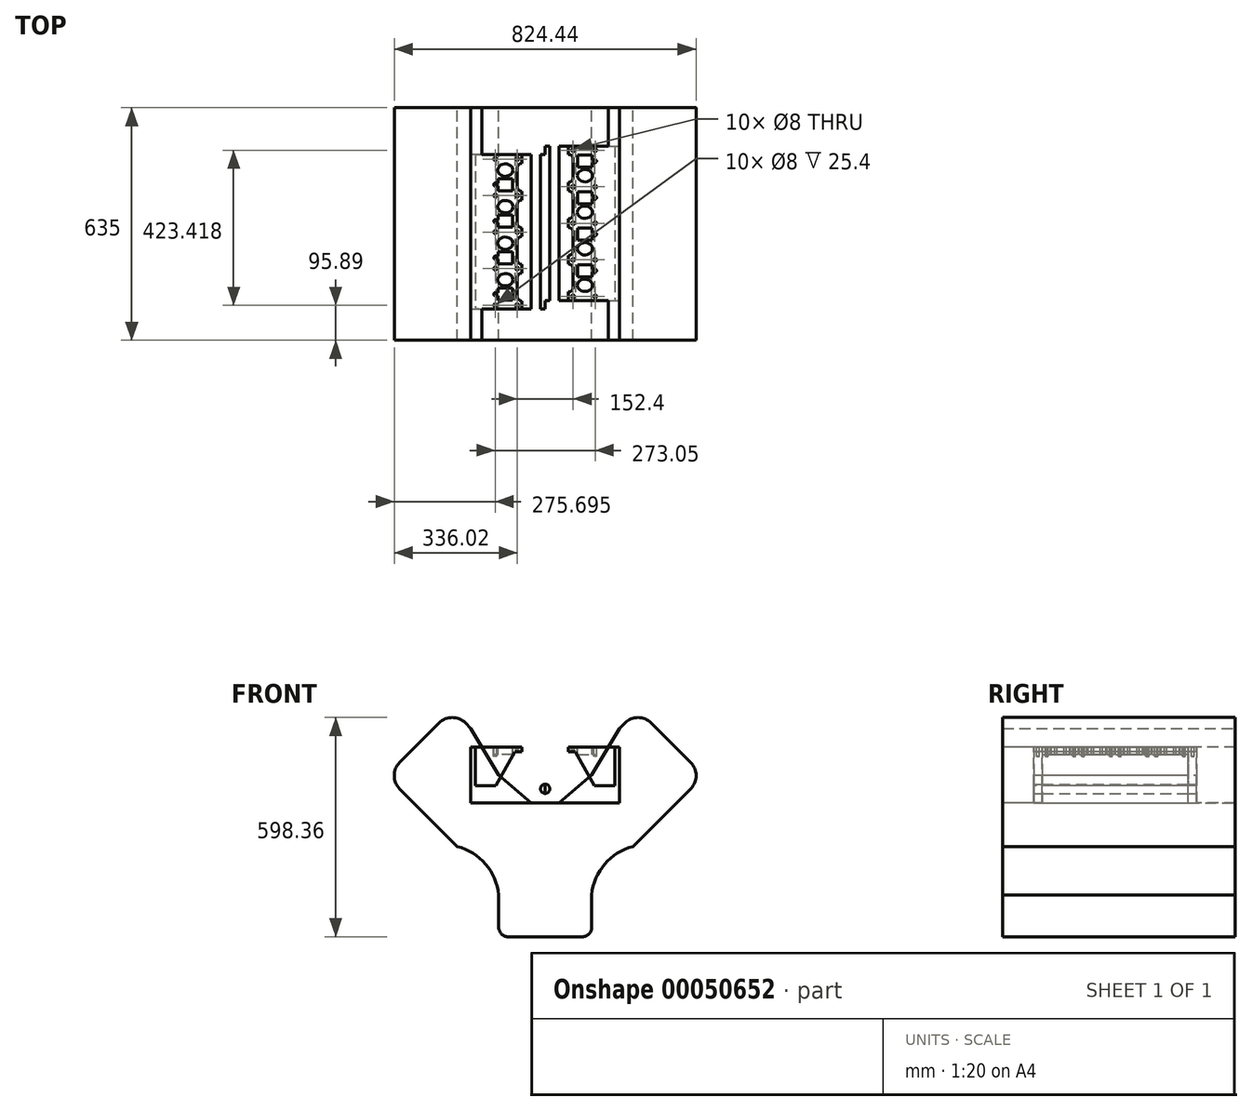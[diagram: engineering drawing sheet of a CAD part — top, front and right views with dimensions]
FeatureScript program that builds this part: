
annotation { "Feature Type Name" : "Feature", "Feature Type Description" : "" }
export const myFeature = defineFeature(function(context is Context, id is Id, definition is map)
    precondition{}
    {
        {
            var Q0;
            Q0=qCreatedBy(makeId("Front.planeOp"),FACE);
            var sketch = newSketch(context, id + "F0", { "sketchPlane" : qUnion([Q0])});
            skLineSegment(sketch, "E0", {"start": v(0, 0) * mm, "end": v(-323.29, 323.29) * mm, "construction": true});
            skLineSegment(sketch, "E1", {"start": v(0, 0) * mm, "end": v(465.39, 465.39) * mm, "construction": true});
            skLineSegment(sketch, "E2", {"start": v(-127, 0) * mm, "end": v(-127, -76.2) * mm});
            skLineSegment(sketch, "E3", {"start": v(-127, -76.2) * mm, "end": v(0, -76.2) * mm, "construction": true});
            skLineSegment(sketch, "E4", {"start": v(-377.17, 269.4) * mm, "end": v(-239.8, 132.03) * mm});
            skLineSegment(sketch, "E5", {"start": v(-203.2, 454.65) * mm, "end": v(-127, 327.65) * mm});
            skLineSegment(sketch, "E6", {"start": v(-127, 327.65) * mm, "end": v(-38.1, 251.45) * mm});
            skLineSegment(sketch, "E7", {"start": v(-38.1, 251.45) * mm, "end": v(0, 251.45) * mm});
            skLineSegment(sketch, "E8", {"start": v(-377.17, 269.4) * mm, "end": v(-397.34, 289.57) * mm});
            skLineSegment(sketch, "E9", {"start": v(-397.34, 361.42) * mm, "end": v(-289.57, 469.18) * mm});
            skLineSegment(sketch, "E10", {"start": v(-203.2, 454.65) * mm, "end": v(-217.73, 469.18) * mm});
            skPoint(sketch, "E11", {"position": v(-323.29, 323.29) * mm});
            skArc(sketch, "E12", {"start": v(-127, 0) * mm, "mid": v(-162.67, 83.72) * mm, "end": v(-239.8, 132.03) * mm});
            skPoint(sketch, "E13.visualSharp", {"position": v(-253.65, 505.1) * mm});
            skArc(sketch, "E13.filletArc", {"start": v(-217.73, 469.18) * mm, "mid": v(-253.65, 484.06) * mm, "end": v(-289.57, 469.18) * mm});
            skPoint(sketch, "E14.visualSharp", {"position": v(-433.26, 325.5) * mm});
            skArc(sketch, "E14.filletArc", {"start": v(-397.34, 361.42) * mm, "mid": v(-412.22, 325.5) * mm, "end": v(-397.34, 289.57) * mm});
            skLineSegment(sketch, "E15.MirrorCS", {"start": v(377.17, 269.4) * mm, "end": v(397.34, 289.57) * mm});
            skLineSegment(sketch, "E16.MirrorCS", {"start": v(203.2, 454.65) * mm, "end": v(217.73, 469.18) * mm});
            skLineSegment(sketch, "E17.MirrorCS", {"start": v(38.1, 251.45) * mm, "end": v(0, 251.45) * mm});
            skArc(sketch, "E18.MirrorCS", {"start": v(217.73, 469.18) * mm, "mid": v(253.65, 484.06) * mm, "end": v(289.57, 469.18) * mm});
            skArc(sketch, "E19.MirrorCS", {"start": v(397.34, 361.42) * mm, "mid": v(412.22, 325.5) * mm, "end": v(397.34, 289.57) * mm});
            skLineSegment(sketch, "E20.MirrorCS", {"start": v(0, 0) * mm, "end": v(323.29, 323.29) * mm, "construction": true});
            skLineSegment(sketch, "E21.MirrorCS", {"start": v(377.17, 269.4) * mm, "end": v(203.2, 454.65) * mm, "construction": true});
            skLineSegment(sketch, "E22.MirrorCS", {"start": v(127, 327.65) * mm, "end": v(38.1, 251.45) * mm});
            skLineSegment(sketch, "E23.MirrorCS", {"start": v(203.2, 454.65) * mm, "end": v(127, 327.65) * mm});
            skPoint(sketch, "E24.MirrorP", {"position": v(253.65, 505.1) * mm});
            skPoint(sketch, "E25.MirrorP", {"position": v(433.26, 325.5) * mm});
            skLineSegment(sketch, "E26.MirrorCS", {"start": v(127, -76.2) * mm, "end": v(0, -76.2) * mm, "construction": true});
            skLineSegment(sketch, "E27.MirrorCS", {"start": v(397.34, 361.42) * mm, "end": v(289.57, 469.18) * mm});
            skPoint(sketch, "E28.MirrorP", {"position": v(323.29, 323.29) * mm});
            skArc(sketch, "E29.MirrorCS", {"start": v(127, 0) * mm, "mid": v(162.67, 83.72) * mm, "end": v(239.8, 132.03) * mm});
            skLineSegment(sketch, "E30.MirrorCS", {"start": v(127, 0) * mm, "end": v(127, -76.2) * mm});
            skLineSegment(sketch, "E31.MirrorCS", {"start": v(377.17, 269.4) * mm, "end": v(239.8, 132.03) * mm});
            skLineSegment(sketch, "E32", {"start": v(-127, -76.2) * mm, "end": v(-127, -88.9) * mm});
            skLineSegment(sketch, "E33", {"start": v(-101.6, -114.3) * mm, "end": v(101.6, -114.3) * mm});
            skLineSegment(sketch, "E34", {"start": v(127, -88.9) * mm, "end": v(127, -76.2) * mm});
            skPoint(sketch, "E35.visualSharp", {"position": v(-127, -114.3) * mm});
            skArc(sketch, "E35.filletArc", {"start": v(-127, -88.9) * mm, "mid": v(-119.56, -106.86) * mm, "end": v(-101.6, -114.3) * mm});
            skPoint(sketch, "E36.visualSharp", {"position": v(127, -114.3) * mm});
            skArc(sketch, "E37.filletArc", {"start": v(101.6, -114.3) * mm, "mid": v(119.56, -106.86) * mm, "end": v(127, -88.9) * mm});
            skSolve(sketch);
        }
        {
            var Q0;
            Q0 = qSketchRegion(id + "F0", true);
            extrude(context, id + "F1", {"entities" : qUnion([Q0]), "depth" : 635 * mm});
        }
        {
            var Q0;
            Q0=makeQuery(id+"F1.opExtrude","CAP_FACE",FACE,{"disambiguationData":[OSD([sQuery(id+"F0.wireOp",EDGE,"E2"),sQuery(id+"F0.wireOp",EDGE,"E4"),sQuery(id+"F0.wireOp",EDGE,"E5"),sQuery(id+"F0.wireOp",EDGE,"E6"),sQuery(id+"F0.wireOp",EDGE,"E7"),sQuery(id+"F0.wireOp",EDGE,"E8"),sQuery(id+"F0.wireOp",EDGE,"E9"),sQuery(id+"F0.wireOp",EDGE,"E10"),sQuery(id+"F0.wireOp",EDGE,"E12"),sQuery(id+"F0.wireOp",EDGE,"E13.filletArc"),sQuery(id+"F0.wireOp",EDGE,"E14.filletArc"),sQuery(id+"F0.wireOp",EDGE,"E15.MirrorCS"),sQuery(id+"F0.wireOp",EDGE,"E16.MirrorCS"),sQuery(id+"F0.wireOp",EDGE,"E17.MirrorCS"),sQuery(id+"F0.wireOp",EDGE,"E18.MirrorCS"),sQuery(id+"F0.wireOp",EDGE,"E19.MirrorCS"),sQuery(id+"F0.wireOp",EDGE,"E22.MirrorCS"),sQuery(id+"F0.wireOp",EDGE,"E23.MirrorCS"),sQuery(id+"F0.wireOp",EDGE,"E27.MirrorCS"),sQuery(id+"F0.wireOp",EDGE,"E29.MirrorCS"),sQuery(id+"F0.wireOp",EDGE,"E30.MirrorCS"),sQuery(id+"F0.wireOp",EDGE,"E31.MirrorCS"),sQuery(id+"F0.wireOp",EDGE,"E32"),sQuery(id+"F0.wireOp",EDGE,"E33"),sQuery(id+"F0.wireOp",EDGE,"E34"),sQuery(id+"F0.wireOp",EDGE,"E35.filletArc"),sQuery(id+"F0.wireOp",EDGE,"E37.filletArc")])],"isStart":false});
            var sketch = newSketch(context, id + "F2", { "sketchPlane" : qUnion([Q0])});
            skLineSegment(sketch, "E38", {"start": v(-121.92, 323.3) * mm, "end": v(-74.71, 323.79) * mm});
            skLineSegment(sketch, "E39", {"start": v(-74.71, 323.79) * mm, "end": v(-50.8, 323.79) * mm});
            skLineSegment(sketch, "E40", {"start": v(-50.8, 323.79) * mm, "end": v(-50.8, 305.32) * mm});
            skLineSegment(sketch, "E41", {"start": v(-50.8, 305.32) * mm, "end": v(0, 298.43) * mm});
            skLineSegment(sketch, "E42", {"start": v(-121.92, 323.3) * mm, "end": v(-38.1, 251.45) * mm});
            skLineSegment(sketch, "E43", {"start": v(-38.1, 251.45) * mm, "end": v(0, 251.45) * mm});
            skLineSegment(sketch, "E44.MirrorCS", {"start": v(50.8, 323.79) * mm, "end": v(50.8, 305.32) * mm});
            skLineSegment(sketch, "E45.MirrorCS", {"start": v(38.1, 251.45) * mm, "end": v(0, 251.45) * mm});
            skLineSegment(sketch, "E46.MirrorCS", {"start": v(121.92, 323.3) * mm, "end": v(38.1, 251.45) * mm});
            skLineSegment(sketch, "E47.MirrorCS", {"start": v(50.8, 305.32) * mm, "end": v(0, 298.43) * mm});
            skLineSegment(sketch, "E48.MirrorCS", {"start": v(74.71, 323.79) * mm, "end": v(50.8, 323.79) * mm});
            skLineSegment(sketch, "E49.MirrorCS", {"start": v(121.92, 323.3) * mm, "end": v(74.71, 323.79) * mm});
            skCircle(sketch, "E50", {"center": v(-63.5, 311.09) * mm, "radius": 4 * mm});
            skCircle(sketch, "E51.MirrorC", {"center": v(63.5, 311.09) * mm, "radius": 4 * mm});
            skSolve(sketch);
        }
        {
            var Q0;
            Q0 = qSketchRegion(id + "F2", true);
            extrude(context, id + "F3", {"entities" : qUnion([Q0]), "oppositeDirection" : true, "depth" : 25.4 * mm});
        }
        {
            var Q0;
            Q0=makeQuery(id+"F1.opExtrude","CAP_FACE",FACE,{"disambiguationData":[OSD([sQuery(id+"F0.wireOp",EDGE,"E2"),sQuery(id+"F0.wireOp",EDGE,"E4"),sQuery(id+"F0.wireOp",EDGE,"E5"),sQuery(id+"F0.wireOp",EDGE,"E6"),sQuery(id+"F0.wireOp",EDGE,"E7"),sQuery(id+"F0.wireOp",EDGE,"E8"),sQuery(id+"F0.wireOp",EDGE,"E9"),sQuery(id+"F0.wireOp",EDGE,"E10"),sQuery(id+"F0.wireOp",EDGE,"E12"),sQuery(id+"F0.wireOp",EDGE,"E13.filletArc"),sQuery(id+"F0.wireOp",EDGE,"E14.filletArc"),sQuery(id+"F0.wireOp",EDGE,"E15.MirrorCS"),sQuery(id+"F0.wireOp",EDGE,"E16.MirrorCS"),sQuery(id+"F0.wireOp",EDGE,"E17.MirrorCS"),sQuery(id+"F0.wireOp",EDGE,"E18.MirrorCS"),sQuery(id+"F0.wireOp",EDGE,"E19.MirrorCS"),sQuery(id+"F0.wireOp",EDGE,"E22.MirrorCS"),sQuery(id+"F0.wireOp",EDGE,"E23.MirrorCS"),sQuery(id+"F0.wireOp",EDGE,"E27.MirrorCS"),sQuery(id+"F0.wireOp",EDGE,"E29.MirrorCS"),sQuery(id+"F0.wireOp",EDGE,"E30.MirrorCS"),sQuery(id+"F0.wireOp",EDGE,"E31.MirrorCS"),sQuery(id+"F0.wireOp",EDGE,"E32"),sQuery(id+"F0.wireOp",EDGE,"E33"),sQuery(id+"F0.wireOp",EDGE,"E34"),sQuery(id+"F0.wireOp",EDGE,"E35.filletArc"),sQuery(id+"F0.wireOp",EDGE,"E37.filletArc")])],"isStart":false});
            cPlane(context, id + "F4", {"entities" : qUnion([Q0]), "cplaneType" : CPlaneType.OFFSET, "offset" : 50.8 * mm, "oppositeDirection" : true, "width" : 152.4 * mm, "height" : 152.4 * mm});
        }
        {
            var Q0;
            Q0=qCreatedBy(id+"F4.planeOp",FACE);
            var sketch = newSketch(context, id + "F5", { "sketchPlane" : qUnion([Q0])});
            skLineSegment(sketch, "E52", {"start": v(-190.5, 403.85) * mm, "end": v(-63.5, 403.85) * mm});
            skLineSegment(sketch, "E53", {"start": v(-63.5, 403.85) * mm, "end": v(-63.5, 391.15) * mm});
            skLineSegment(sketch, "E54", {"start": v(-63.5, 391.15) * mm, "end": v(-82.55, 391.15) * mm});
            skLineSegment(sketch, "E55", {"start": v(-82.55, 391.15) * mm, "end": v(-134.69, 298.45) * mm});
            skLineSegment(sketch, "E56", {"start": v(-190.5, 403.85) * mm, "end": v(-190.5, 298.45) * mm});
            skLineSegment(sketch, "E57", {"start": v(-190.5, 298.45) * mm, "end": v(-134.69, 298.45) * mm});
            skLineSegment(sketch, "E58.MirrorCS", {"start": v(82.55, 391.15) * mm, "end": v(134.69, 298.45) * mm});
            skLineSegment(sketch, "E59.MirrorCS", {"start": v(190.5, 403.85) * mm, "end": v(190.5, 298.45) * mm});
            skLineSegment(sketch, "E60.MirrorCS", {"start": v(190.5, 298.45) * mm, "end": v(134.69, 298.45) * mm});
            skLineSegment(sketch, "E61.MirrorCS", {"start": v(190.5, 403.85) * mm, "end": v(63.5, 403.85) * mm});
            skLineSegment(sketch, "E62.MirrorCS", {"start": v(63.5, 391.15) * mm, "end": v(82.55, 391.15) * mm});
            skLineSegment(sketch, "E63.MirrorCS", {"start": v(63.5, 403.85) * mm, "end": v(63.5, 391.15) * mm});
            skSolve(sketch);
        }
        {
            var Q0;
            Q0=qCreatedBy(id+"F4.planeOp",FACE);
            var sketch = newSketch(context, id + "F6", { "sketchPlane" : qUnion([Q0])});
            skCircle(sketch, "E64", {"center": v(0, 289.55) * mm, "radius": 12.7 * mm});
            skSolve(sketch);
        }
        {
            var Q0;
            Q0 = qSketchRegion(id + "F6", true);
            extrude(context, id + "F7", {"entities" : qUnion([Q0]), "operationType" : NewBodyOperationType.ADD, "depth" : 25.4 * mm});
        }
        {
            var Q0;
            Q0 = qSketchRegion(id + "F6", true);
            var Q1;
            Q1=makeQuery(id+"F1.opExtrude","CAP_FACE",FACE,{"disambiguationData":[OSD([sQuery(id+"F0.wireOp",EDGE,"E2"),sQuery(id+"F0.wireOp",EDGE,"E4"),sQuery(id+"F0.wireOp",EDGE,"E5"),sQuery(id+"F0.wireOp",EDGE,"E6"),sQuery(id+"F0.wireOp",EDGE,"E7"),sQuery(id+"F0.wireOp",EDGE,"E8"),sQuery(id+"F0.wireOp",EDGE,"E9"),sQuery(id+"F0.wireOp",EDGE,"E10"),sQuery(id+"F0.wireOp",EDGE,"E12"),sQuery(id+"F0.wireOp",EDGE,"E13.filletArc"),sQuery(id+"F0.wireOp",EDGE,"E14.filletArc"),sQuery(id+"F0.wireOp",EDGE,"E15.MirrorCS"),sQuery(id+"F0.wireOp",EDGE,"E16.MirrorCS"),sQuery(id+"F0.wireOp",EDGE,"E17.MirrorCS"),sQuery(id+"F0.wireOp",EDGE,"E18.MirrorCS"),sQuery(id+"F0.wireOp",EDGE,"E19.MirrorCS"),sQuery(id+"F0.wireOp",EDGE,"E22.MirrorCS"),sQuery(id+"F0.wireOp",EDGE,"E23.MirrorCS"),sQuery(id+"F0.wireOp",EDGE,"E27.MirrorCS"),sQuery(id+"F0.wireOp",EDGE,"E29.MirrorCS"),sQuery(id+"F0.wireOp",EDGE,"E30.MirrorCS"),sQuery(id+"F0.wireOp",EDGE,"E31.MirrorCS"),sQuery(id+"F0.wireOp",EDGE,"E32"),sQuery(id+"F0.wireOp",EDGE,"E33"),sQuery(id+"F0.wireOp",EDGE,"E34"),sQuery(id+"F0.wireOp",EDGE,"E35.filletArc"),sQuery(id+"F0.wireOp",EDGE,"E37.filletArc")])],"isStart":true});
            extrude(context, id + "F8", {"entities" : qUnion([Q0]), "operationType" : NewBodyOperationType.ADD, "endBound" : BoundingType.UP_TO_SURFACE, "oppositeDirection" : true, "endBoundEntityFace" : qUnion([Q1]), "depth" : 25.4 * mm});
        }
        {
            var Q0;
            Q0 = qSketchRegion(id + "F5", true);
            extrude(context, id + "F9", {"entities" : qUnion([Q0]), "oppositeDirection" : true, "depth" : 558.8 * mm});
        }
        {
            var Q0;
            Q0=makeQuery(id+"F9.opExtrude","SWEPT_FACE",FACE,{"disambiguationData":[OSD([sQuery(id+"F5.wireOp",EDGE,"E52")])]});
            var sketch = newSketch(context, id + "F10", { "sketchPlane" : qUnion([Q0])});
            skCircle(sketch, "E65", {"center": v(-108.71, -170.05) * mm, "radius": 19.05 * mm, "construction": true});
            skLineSegment(sketch, "E66", {"start": v(-108.71, -170.05) * mm, "end": v(-108.71, -861.46) * mm, "construction": true});
            skLineSegment(sketch, "E67.rect.bottom", {"start": v(-88.9, -226.3) * mm, "end": v(-128.52, -226.3) * mm});
            skLineSegment(sketch, "E67.rect.top", {"start": v(-88.9, -193.29) * mm, "end": v(-128.52, -193.29) * mm});
            skLineSegment(sketch, "E67.rect.left", {"start": v(-88.9, -226.3) * mm, "end": v(-88.9, -193.29) * mm});
            skLineSegment(sketch, "E67.rect.right", {"start": v(-128.52, -226.3) * mm, "end": v(-128.52, -214.24) * mm});
            skPoint(sketch, "E67.rect.middle", {"position": v(-108.71, -209.8) * mm});
            skArc(sketch, "E68", {"start": v(-136.02, -205.35) * mm, "mid": v(-140.46, -209.8) * mm, "end": v(-136.02, -214.24) * mm});
            skPoint(sketch, "E68.centerSnap0", {"position": v(-128.52, -209.8) * mm});
            skLineSegment(sketch, "E69", {"start": v(-136.02, -205.35) * mm, "end": v(-128.52, -205.35) * mm});
            skLineSegment(sketch, "E70", {"start": v(-136.02, -214.24) * mm, "end": v(-128.52, -214.24) * mm});
            skLineSegment(sketch, "E71.trimOffspring", {"start": v(-128.52, -205.35) * mm, "end": v(-128.52, -193.29) * mm});
            skLineSegment(sketch, "E72.direction1", {"start": v(-108.71, -170.05) * mm, "end": v(-108.62, -284.35) * mm, "construction": true});
            skLineSegment(sketch, "E73.bottom", {"start": v(-63.5, -151.82) * mm, "end": v(-50.69, -151.82) * mm});
            skLineSegment(sketch, "E73.top", {"start": v(-63.5, -228.02) * mm, "end": v(-50.69, -228.02) * mm});
            skLineSegment(sketch, "E73.left", {"start": v(-76.2, -164.52) * mm, "end": v(-76.2, -215.32) * mm});
            skLineSegment(sketch, "E73.right", {"start": v(-50.69, -151.82) * mm, "end": v(-50.69, -228.02) * mm});
            skLineSegment(sketch, "E74", {"start": v(-108.71, -170.05) * mm, "end": v(-108.71, -209.8) * mm, "construction": true});
            skPoint(sketch, "E75", {"position": v(-108.71, -189.92) * mm});
            skLineSegment(sketch, "E76", {"start": v(-108.71, -189.92) * mm, "end": v(-76.2, -189.92) * mm, "construction": true});
            skPoint(sketch, "E77", {"position": v(-76.2, -189.92) * mm});
            skArc(sketch, "E78.filletArc", {"start": v(-76.2, -215.32) * mm, "mid": v(-72.48, -224.3) * mm, "end": v(-63.5, -228.02) * mm});
            skPoint(sketch, "E79.visualSharp", {"position": v(-76.2, -151.82) * mm});
            skArc(sketch, "E79.filletArc", {"start": v(-63.5, -151.82) * mm, "mid": v(-72.48, -155.54) * mm, "end": v(-76.2, -164.52) * mm});
            skLineSegment(sketch, "E80.direction1", {"start": v(-63.5, -228.02) * mm, "end": v(-63.52, -342.32) * mm, "construction": true});
            skPoint(sketch, "E81.center", {"position": v(0, -327.4) * mm});
            skEllipse(sketch, "E82", {"center": v(-108.71, -170.05) * mm, "majorRadius": 20.7 * mm, "minorRadius": 16.9 * mm, "majorAxis": v(1, 0)});
            skLineSegment(sketch, "E83.0.1.0", {"start": v(-63.5, -327.85) * mm, "end": v(-50.69, -327.85) * mm});
            skPoint(sketch, "E83.0.1.1", {"position": v(-108.71, -309.62) * mm});
            skLineSegment(sketch, "E83.0.1.2", {"start": v(-108.71, -289.75) * mm, "end": v(-76.2, -289.75) * mm, "construction": true});
            skArc(sketch, "E83.0.1.3", {"start": v(-63.5, -251.65) * mm, "mid": v(-72.48, -255.37) * mm, "end": v(-76.2, -264.35) * mm});
            skPoint(sketch, "E83.0.1.4", {"position": v(-108.71, -289.75) * mm});
            skCircle(sketch, "E83.0.1.5", {"center": v(-108.71, -269.87) * mm, "radius": 19.05 * mm, "construction": true});
            skLineSegment(sketch, "E83.0.1.6", {"start": v(-50.69, -251.65) * mm, "end": v(-50.69, -327.85) * mm});
            skArc(sketch, "E83.0.1.7", {"start": v(-76.2, -315.15) * mm, "mid": v(-72.48, -324.13) * mm, "end": v(-63.5, -327.85) * mm});
            skLineSegment(sketch, "E83.0.1.8", {"start": v(-128.52, -305.18) * mm, "end": v(-128.52, -293.11) * mm});
            skLineSegment(sketch, "E83.0.1.9", {"start": v(-88.9, -326.13) * mm, "end": v(-128.52, -326.13) * mm});
            skLineSegment(sketch, "E83.0.1.10", {"start": v(-108.71, -269.87) * mm, "end": v(-108.71, -309.62) * mm, "construction": true});
            skArc(sketch, "E83.0.1.11", {"start": v(-136.02, -305.18) * mm, "mid": v(-140.46, -309.62) * mm, "end": v(-136.02, -314.07) * mm});
            skLineSegment(sketch, "E83.0.1.12", {"start": v(-76.2, -264.35) * mm, "end": v(-76.2, -315.15) * mm});
            skEllipse(sketch, "E83.0.1.13", {"center": v(-108.71, -269.87) * mm, "majorRadius": 20.7 * mm, "minorRadius": 16.9 * mm, "majorAxis": v(1, 0)});
            skPoint(sketch, "E83.0.1.14", {"position": v(-76.2, -289.75) * mm});
            skLineSegment(sketch, "E83.0.1.15", {"start": v(-63.5, -251.65) * mm, "end": v(-50.69, -251.65) * mm});
            skPoint(sketch, "E83.0.1.16", {"position": v(-76.2, -251.65) * mm});
            skPoint(sketch, "E83.0.1.17", {"position": v(-128.52, -309.62) * mm});
            skLineSegment(sketch, "E83.0.1.18", {"start": v(-88.9, -293.11) * mm, "end": v(-128.52, -293.11) * mm});
            skLineSegment(sketch, "E83.0.1.19", {"start": v(-88.9, -326.13) * mm, "end": v(-88.9, -293.11) * mm});
            skLineSegment(sketch, "E83.0.1.20", {"start": v(-128.52, -326.13) * mm, "end": v(-128.52, -314.07) * mm});
            skPoint(sketch, "E83.0.1.21", {"position": v(-76.2, -289.75) * mm});
            skLineSegment(sketch, "E83.0.1.22", {"start": v(-136.02, -314.07) * mm, "end": v(-128.52, -314.07) * mm});
            skLineSegment(sketch, "E83.0.1.23", {"start": v(-136.02, -305.18) * mm, "end": v(-128.52, -305.18) * mm});
            skLineSegment(sketch, "E83.0.2.0", {"start": v(-63.5, -427.67) * mm, "end": v(-50.69, -427.67) * mm});
            skPoint(sketch, "E83.0.2.1", {"position": v(-108.71, -409.44) * mm});
            skLineSegment(sketch, "E83.0.2.2", {"start": v(-108.71, -389.57) * mm, "end": v(-76.2, -389.57) * mm, "construction": true});
            skArc(sketch, "E83.0.2.3", {"start": v(-63.5, -351.47) * mm, "mid": v(-72.48, -355.19) * mm, "end": v(-76.2, -364.17) * mm});
            skPoint(sketch, "E83.0.2.4", {"position": v(-108.71, -389.57) * mm});
            skCircle(sketch, "E83.0.2.5", {"center": v(-108.71, -369.7) * mm, "radius": 19.05 * mm, "construction": true});
            skLineSegment(sketch, "E83.0.2.6", {"start": v(-50.69, -351.47) * mm, "end": v(-50.69, -427.67) * mm});
            skArc(sketch, "E83.0.2.7", {"start": v(-76.2, -414.97) * mm, "mid": v(-72.48, -423.95) * mm, "end": v(-63.5, -427.67) * mm});
            skLineSegment(sketch, "E83.0.2.8", {"start": v(-128.52, -405) * mm, "end": v(-128.52, -392.93) * mm});
            skLineSegment(sketch, "E83.0.2.9", {"start": v(-88.9, -425.95) * mm, "end": v(-128.52, -425.95) * mm});
            skLineSegment(sketch, "E83.0.2.10", {"start": v(-108.71, -369.7) * mm, "end": v(-108.71, -409.44) * mm, "construction": true});
            skArc(sketch, "E83.0.2.11", {"start": v(-136.02, -405) * mm, "mid": v(-140.46, -409.44) * mm, "end": v(-136.02, -413.89) * mm});
            skLineSegment(sketch, "E83.0.2.12", {"start": v(-76.2, -364.17) * mm, "end": v(-76.2, -414.97) * mm});
            skEllipse(sketch, "E83.0.2.13", {"center": v(-108.71, -369.7) * mm, "majorRadius": 20.7 * mm, "minorRadius": 16.9 * mm, "majorAxis": v(1, 0)});
            skPoint(sketch, "E83.0.2.14", {"position": v(-76.2, -389.57) * mm});
            skLineSegment(sketch, "E83.0.2.15", {"start": v(-63.5, -351.47) * mm, "end": v(-50.69, -351.47) * mm});
            skPoint(sketch, "E83.0.2.16", {"position": v(-76.2, -351.47) * mm});
            skPoint(sketch, "E83.0.2.17", {"position": v(-128.52, -409.44) * mm});
            skLineSegment(sketch, "E83.0.2.18", {"start": v(-88.9, -392.93) * mm, "end": v(-128.52, -392.93) * mm});
            skLineSegment(sketch, "E83.0.2.19", {"start": v(-88.9, -425.95) * mm, "end": v(-88.9, -392.93) * mm});
            skLineSegment(sketch, "E83.0.2.20", {"start": v(-128.52, -425.95) * mm, "end": v(-128.52, -413.89) * mm});
            skPoint(sketch, "E83.0.2.21", {"position": v(-76.2, -389.57) * mm});
            skLineSegment(sketch, "E83.0.2.22", {"start": v(-136.02, -413.89) * mm, "end": v(-128.52, -413.89) * mm});
            skLineSegment(sketch, "E83.0.2.23", {"start": v(-136.02, -405) * mm, "end": v(-128.52, -405) * mm});
            skLineSegment(sketch, "E83.0.3.0", {"start": v(-63.5, -527.49) * mm, "end": v(-50.69, -527.49) * mm});
            skPoint(sketch, "E83.0.3.1", {"position": v(-108.71, -509.27) * mm});
            skLineSegment(sketch, "E83.0.3.2", {"start": v(-108.71, -489.39) * mm, "end": v(-76.2, -489.39) * mm, "construction": true});
            skArc(sketch, "E83.0.3.3", {"start": v(-63.5, -451.29) * mm, "mid": v(-72.48, -455) * mm, "end": v(-76.2, -463.99) * mm});
            skPoint(sketch, "E83.0.3.4", {"position": v(-108.71, -489.39) * mm});
            skCircle(sketch, "E83.0.3.5", {"center": v(-108.71, -469.51) * mm, "radius": 19.05 * mm, "construction": true});
            skLineSegment(sketch, "E83.0.3.6", {"start": v(-50.69, -451.29) * mm, "end": v(-50.69, -527.49) * mm});
            skArc(sketch, "E83.0.3.7", {"start": v(-76.2, -514.79) * mm, "mid": v(-72.48, -523.77) * mm, "end": v(-63.5, -527.49) * mm});
            skLineSegment(sketch, "E83.0.3.8", {"start": v(-128.52, -504.82) * mm, "end": v(-128.52, -492.76) * mm});
            skLineSegment(sketch, "E83.0.3.9", {"start": v(-88.9, -525.78) * mm, "end": v(-128.52, -525.78) * mm});
            skLineSegment(sketch, "E83.0.3.10", {"start": v(-108.71, -469.51) * mm, "end": v(-108.71, -509.27) * mm, "construction": true});
            skArc(sketch, "E83.0.3.11", {"start": v(-136.02, -504.82) * mm, "mid": v(-140.46, -509.27) * mm, "end": v(-136.02, -513.71) * mm});
            skLineSegment(sketch, "E83.0.3.12", {"start": v(-76.2, -463.99) * mm, "end": v(-76.2, -514.79) * mm});
            skEllipse(sketch, "E83.0.3.13", {"center": v(-108.71, -469.51) * mm, "majorRadius": 20.7 * mm, "minorRadius": 16.9 * mm, "majorAxis": v(1, 0)});
            skPoint(sketch, "E83.0.3.14", {"position": v(-76.2, -489.39) * mm});
            skLineSegment(sketch, "E83.0.3.15", {"start": v(-63.5, -451.29) * mm, "end": v(-50.69, -451.29) * mm});
            skPoint(sketch, "E83.0.3.16", {"position": v(-76.2, -451.29) * mm});
            skPoint(sketch, "E83.0.3.17", {"position": v(-128.52, -509.27) * mm});
            skLineSegment(sketch, "E83.0.3.18", {"start": v(-88.9, -492.76) * mm, "end": v(-128.52, -492.76) * mm});
            skLineSegment(sketch, "E83.0.3.19", {"start": v(-88.9, -525.78) * mm, "end": v(-88.9, -492.76) * mm});
            skLineSegment(sketch, "E83.0.3.20", {"start": v(-128.52, -525.78) * mm, "end": v(-128.52, -513.71) * mm});
            skPoint(sketch, "E83.0.3.21", {"position": v(-76.2, -489.39) * mm});
            skLineSegment(sketch, "E83.0.3.22", {"start": v(-136.02, -513.71) * mm, "end": v(-128.52, -513.71) * mm});
            skLineSegment(sketch, "E83.0.3.23", {"start": v(-136.02, -504.82) * mm, "end": v(-128.52, -504.82) * mm});
            skLineSegment(sketch, "E83.direction1", {"start": v(-63.5, -228.02) * mm, "end": v(-38.1, -228.02) * mm, "construction": true});
            skLineSegment(sketch, "E83.direction2", {"start": v(-63.5, -228.02) * mm, "end": v(-63.5, -327.85) * mm, "construction": true});
            skPoint(sketch, "E84.1.0", {"position": v(108.71, -265.23) * mm});
            skPoint(sketch, "E84.1.1", {"position": v(76.2, -203.51) * mm});
            skCircle(sketch, "E84.1.2", {"center": v(108.71, -285.11) * mm, "radius": 19.05 * mm, "construction": true});
            skLineSegment(sketch, "E84.1.3", {"start": v(88.9, -328.67) * mm, "end": v(128.52, -328.67) * mm});
            skArc(sketch, "E84.1.4", {"start": v(76.2, -339.66) * mm, "mid": v(72.48, -330.68) * mm, "end": v(63.5, -326.96) * mm});
            skLineSegment(sketch, "E84.1.5", {"start": v(76.2, -190.81) * mm, "end": v(76.2, -140.01) * mm});
            skEllipse(sketch, "E84.1.6", {"center": v(108.71, -484.75) * mm, "majorRadius": 20.7 * mm, "minorRadius": 16.9 * mm, "majorAxis": v(-1, 0)});
            skPoint(sketch, "E84.1.7", {"position": v(128.52, -245.36) * mm});
            skLineSegment(sketch, "E84.1.8", {"start": v(50.69, -303.33) * mm, "end": v(50.69, -227.13) * mm});
            skPoint(sketch, "E84.1.9", {"position": v(108.71, -445) * mm});
            skCircle(sketch, "E84.1.10", {"center": v(108.71, -484.75) * mm, "radius": 19.05 * mm, "construction": true});
            skLineSegment(sketch, "E84.1.11", {"start": v(76.2, -290.63) * mm, "end": v(76.2, -239.83) * mm});
            skLineSegment(sketch, "E84.1.12", {"start": v(76.2, -390.46) * mm, "end": v(76.2, -339.66) * mm});
            skPoint(sketch, "E84.1.13", {"position": v(108.71, -345.18) * mm});
            skPoint(sketch, "E84.1.14", {"position": v(76.2, -464.88) * mm});
            skPoint(sketch, "E84.1.15", {"position": v(76.2, -365.06) * mm});
            skPoint(sketch, "E84.1.16", {"position": v(76.2, -165.41) * mm});
            skLineSegment(sketch, "E84.1.17", {"start": v(88.9, -428.5) * mm, "end": v(88.9, -461.51) * mm});
            skLineSegment(sketch, "E84.1.18", {"start": v(88.9, -228.85) * mm, "end": v(128.52, -228.85) * mm});
            skLineSegment(sketch, "E84.1.19", {"start": v(88.9, -228.85) * mm, "end": v(88.9, -261.87) * mm});
            skArc(sketch, "E84.1.20", {"start": v(76.2, -140.01) * mm, "mid": v(72.48, -131.03) * mm, "end": v(63.5, -127.31) * mm});
            skPoint(sketch, "E84.1.21", {"position": v(108.71, -464.88) * mm});
            skPoint(sketch, "E84.1.22", {"position": v(76.2, -403.16) * mm});
            skPoint(sketch, "E84.1.23", {"position": v(108.71, -165.41) * mm});
            skPoint(sketch, "E84.1.24", {"position": v(128.52, -145.54) * mm});
            skLineSegment(sketch, "E84.1.25", {"start": v(88.9, -129.03) * mm, "end": v(88.9, -162.05) * mm});
            skLineSegment(sketch, "E84.1.26", {"start": v(63.5, -426.78) * mm, "end": v(63.5, -326.96) * mm, "construction": true});
            skLineSegment(sketch, "E84.1.27", {"start": v(88.9, -129.03) * mm, "end": v(128.52, -129.03) * mm});
            skPoint(sketch, "E84.1.28", {"position": v(128.52, -345.18) * mm});
            skCircle(sketch, "E84.1.29", {"center": v(108.71, -185.29) * mm, "radius": 19.05 * mm, "construction": true});
            skLineSegment(sketch, "E84.1.30", {"start": v(108.71, -484.75) * mm, "end": v(108.62, -370.45) * mm, "construction": true});
            skLineSegment(sketch, "E84.1.31", {"start": v(50.69, -203.51) * mm, "end": v(50.69, -127.31) * mm});
            skEllipse(sketch, "E84.1.32", {"center": v(108.71, -185.29) * mm, "majorRadius": 20.7 * mm, "minorRadius": 16.9 * mm, "majorAxis": v(-1, 0)});
            skLineSegment(sketch, "E84.1.33", {"start": v(50.69, -502.98) * mm, "end": v(50.69, -426.78) * mm});
            skPoint(sketch, "E84.1.34", {"position": v(128.52, -445) * mm});
            skPoint(sketch, "E84.1.35", {"position": v(108.71, -145.54) * mm});
            skPoint(sketch, "E84.1.36", {"position": v(76.2, -265.23) * mm});
            skEllipse(sketch, "E84.1.37", {"center": v(108.71, -384.93) * mm, "majorRadius": 20.7 * mm, "minorRadius": 16.9 * mm, "majorAxis": v(-1, 0)});
            skArc(sketch, "E84.1.38", {"start": v(76.2, -239.83) * mm, "mid": v(72.48, -230.85) * mm, "end": v(63.5, -227.13) * mm});
            skLineSegment(sketch, "E84.1.39", {"start": v(50.69, -403.16) * mm, "end": v(50.69, -326.96) * mm});
            skPoint(sketch, "E84.1.40", {"position": v(108.71, -365.06) * mm});
            skPoint(sketch, "E84.1.41", {"position": v(108.71, -245.36) * mm});
            skPoint(sketch, "E84.1.42", {"position": v(76.2, -502.98) * mm});
            skCircle(sketch, "E84.1.43", {"center": v(108.71, -384.93) * mm, "radius": 19.05 * mm, "construction": true});
            skEllipse(sketch, "E84.1.44", {"center": v(108.71, -285.11) * mm, "majorRadius": 20.7 * mm, "minorRadius": 16.9 * mm, "majorAxis": v(-1, 0)});
            skPoint(sketch, "E84.1.45", {"position": v(76.2, -303.33) * mm});
            skLineSegment(sketch, "E84.1.46", {"start": v(108.71, -165.41) * mm, "end": v(76.2, -165.41) * mm, "construction": true});
            skPoint(sketch, "E84.1.47", {"position": v(76.2, -365.06) * mm});
            skLineSegment(sketch, "E84.1.48", {"start": v(76.2, -490.28) * mm, "end": v(76.2, -439.48) * mm});
            skLineSegment(sketch, "E84.1.49", {"start": v(63.5, -426.78) * mm, "end": v(38.1, -426.78) * mm, "construction": true});
            skLineSegment(sketch, "E84.1.50", {"start": v(63.5, -426.78) * mm, "end": v(63.52, -312.48) * mm, "construction": true});
            skLineSegment(sketch, "E84.1.51", {"start": v(88.9, -261.87) * mm, "end": v(128.52, -261.87) * mm});
            skLineSegment(sketch, "E84.1.52", {"start": v(108.71, -384.93) * mm, "end": v(108.71, -345.18) * mm, "construction": true});
            skArc(sketch, "E84.1.53", {"start": v(63.5, -203.51) * mm, "mid": v(72.48, -199.8) * mm, "end": v(76.2, -190.81) * mm});
            skLineSegment(sketch, "E84.1.54", {"start": v(88.9, -428.5) * mm, "end": v(128.52, -428.5) * mm});
            skLineSegment(sketch, "E84.1.55", {"start": v(108.71, -464.88) * mm, "end": v(76.2, -464.88) * mm, "construction": true});
            skLineSegment(sketch, "E84.1.56", {"start": v(108.71, -285.11) * mm, "end": v(108.71, -245.36) * mm, "construction": true});
            skLineSegment(sketch, "E84.1.57", {"start": v(88.9, -162.05) * mm, "end": v(128.52, -162.05) * mm});
            skLineSegment(sketch, "E84.1.58", {"start": v(108.71, -365.06) * mm, "end": v(76.2, -365.06) * mm, "construction": true});
            skLineSegment(sketch, "E84.1.59", {"start": v(108.71, -185.29) * mm, "end": v(108.71, -145.54) * mm, "construction": true});
            skArc(sketch, "E84.1.60", {"start": v(63.5, -303.33) * mm, "mid": v(72.48, -299.62) * mm, "end": v(76.2, -290.63) * mm});
            skPoint(sketch, "E84.1.61", {"position": v(76.2, -464.88) * mm});
            skLineSegment(sketch, "E84.1.62", {"start": v(88.9, -328.67) * mm, "end": v(88.9, -361.7) * mm});
            skPoint(sketch, "E84.1.63", {"position": v(76.2, -165.41) * mm});
            skLineSegment(sketch, "E84.1.64", {"start": v(108.71, -484.75) * mm, "end": v(108.71, -445) * mm, "construction": true});
            skLineSegment(sketch, "E84.1.65", {"start": v(88.9, -461.51) * mm, "end": v(128.52, -461.51) * mm});
            skPoint(sketch, "E84.1.66", {"position": v(76.2, -265.23) * mm});
            skArc(sketch, "E84.1.67", {"start": v(76.2, -439.48) * mm, "mid": v(72.48, -430.5) * mm, "end": v(63.5, -426.78) * mm});
            skArc(sketch, "E84.1.68", {"start": v(63.5, -403.16) * mm, "mid": v(72.48, -399.44) * mm, "end": v(76.2, -390.46) * mm});
            skLineSegment(sketch, "E84.1.69", {"start": v(108.71, -265.23) * mm, "end": v(76.2, -265.23) * mm, "construction": true});
            skArc(sketch, "E84.1.70", {"start": v(63.5, -502.98) * mm, "mid": v(72.48, -499.26) * mm, "end": v(76.2, -490.28) * mm});
            skLineSegment(sketch, "E84.1.71", {"start": v(88.9, -361.7) * mm, "end": v(128.52, -361.7) * mm});
            skLineSegment(sketch, "E84.1.72", {"start": v(128.52, -349.63) * mm, "end": v(128.52, -361.7) * mm});
            skLineSegment(sketch, "E84.1.73", {"start": v(63.5, -303.33) * mm, "end": v(50.69, -303.33) * mm});
            skLineSegment(sketch, "E84.1.74", {"start": v(128.52, -249.8) * mm, "end": v(128.52, -261.87) * mm});
            skLineSegment(sketch, "E84.1.75", {"start": v(128.52, -328.67) * mm, "end": v(128.52, -340.74) * mm});
            skLineSegment(sketch, "E84.1.76", {"start": v(128.52, -449.45) * mm, "end": v(128.52, -461.51) * mm});
            skArc(sketch, "E84.1.77", {"start": v(136.02, -249.8) * mm, "mid": v(140.46, -245.36) * mm, "end": v(136.02, -240.91) * mm});
            skLineSegment(sketch, "E84.1.78", {"start": v(128.52, -228.85) * mm, "end": v(128.52, -240.91) * mm});
            skLineSegment(sketch, "E84.1.79", {"start": v(128.52, -149.98) * mm, "end": v(128.52, -162.05) * mm});
            skLineSegment(sketch, "E84.1.80", {"start": v(128.52, -428.5) * mm, "end": v(128.52, -440.56) * mm});
            skLineSegment(sketch, "E84.1.81", {"start": v(63.5, -502.98) * mm, "end": v(50.69, -502.98) * mm});
            skArc(sketch, "E84.1.82", {"start": v(136.02, -449.45) * mm, "mid": v(140.46, -445) * mm, "end": v(136.02, -440.56) * mm});
            skLineSegment(sketch, "E84.1.83", {"start": v(63.5, -127.31) * mm, "end": v(50.69, -127.31) * mm});
            skLineSegment(sketch, "E84.1.84", {"start": v(63.5, -203.51) * mm, "end": v(50.69, -203.51) * mm});
            skLineSegment(sketch, "E84.1.85", {"start": v(63.5, -326.96) * mm, "end": v(50.69, -326.96) * mm});
            skLineSegment(sketch, "E84.1.86", {"start": v(63.5, -426.78) * mm, "end": v(50.69, -426.78) * mm});
            skLineSegment(sketch, "E84.1.87", {"start": v(63.5, -227.13) * mm, "end": v(50.69, -227.13) * mm});
            skArc(sketch, "E84.1.88", {"start": v(136.02, -349.63) * mm, "mid": v(140.46, -345.18) * mm, "end": v(136.02, -340.74) * mm});
            skLineSegment(sketch, "E84.1.89", {"start": v(63.5, -403.16) * mm, "end": v(50.69, -403.16) * mm});
            skLineSegment(sketch, "E84.1.90", {"start": v(128.52, -129.03) * mm, "end": v(128.52, -141.1) * mm});
            skArc(sketch, "E84.1.91", {"start": v(136.02, -149.98) * mm, "mid": v(140.46, -145.54) * mm, "end": v(136.02, -141.1) * mm});
            skLineSegment(sketch, "E84.1.92", {"start": v(136.02, -149.98) * mm, "end": v(128.52, -149.98) * mm});
            skLineSegment(sketch, "E84.1.93", {"start": v(136.02, -340.74) * mm, "end": v(128.52, -340.74) * mm});
            skLineSegment(sketch, "E84.1.94", {"start": v(136.02, -141.1) * mm, "end": v(128.52, -141.1) * mm});
            skLineSegment(sketch, "E84.1.95", {"start": v(136.02, -240.91) * mm, "end": v(128.52, -240.91) * mm});
            skLineSegment(sketch, "E84.1.96", {"start": v(136.02, -349.63) * mm, "end": v(128.52, -349.63) * mm});
            skLineSegment(sketch, "E84.1.97", {"start": v(136.02, -440.56) * mm, "end": v(128.52, -440.56) * mm});
            skLineSegment(sketch, "E84.1.98", {"start": v(136.02, -449.45) * mm, "end": v(128.52, -449.45) * mm});
            skLineSegment(sketch, "E84.1.99", {"start": v(136.02, -249.8) * mm, "end": v(128.52, -249.8) * mm});
            skPoint(sketch, "E85", {"position": v(108.71, -501.65) * mm});
            skSolve(sketch);
        }
        {
            var Q0;
            Q0 = qSketchRegion(id + "F10", true);
            extrude(context, id + "F11", {"entities" : qUnion([Q0]), "operationType" : NewBodyOperationType.REMOVE, "oppositeDirection" : true, "depth" : 20.32 * mm});
        }
        {
            var Q0;
            Q0=makeQuery(id+"F9.opExtrude","SWEPT_FACE",FACE,{"disambiguationData":[OSD([sQuery(id+"F5.wireOp",EDGE,"E52")])]});
            var sketch = newSketch(context, id + "F12", { "sketchPlane" : qUnion([Q0])});
            skLineSegment(sketch, "E86.bottom", {"start": v(0, -127.95) * mm, "end": v(-203.2, -127.95) * mm});
            skLineSegment(sketch, "E86.top", {"start": v(0, 0) * mm, "end": v(-203.2, 0) * mm});
            skLineSegment(sketch, "E86.left", {"start": v(0, -127.95) * mm, "end": v(0, 0) * mm});
            skLineSegment(sketch, "E86.right", {"start": v(-203.2, -127.95) * mm, "end": v(-203.2, 0) * mm});
            skLineSegment(sketch, "E87.bottom", {"start": v(0, -526.85) * mm, "end": v(203.2, -526.85) * mm});
            skLineSegment(sketch, "E87.top", {"start": v(0, -653.1) * mm, "end": v(203.2, -653.1) * mm});
            skLineSegment(sketch, "E87.left", {"start": v(0, -526.85) * mm, "end": v(0, -653.1) * mm});
            skLineSegment(sketch, "E87.right", {"start": v(203.2, -526.85) * mm, "end": v(203.2, -653.1) * mm});
            skLineSegment(sketch, "E88.bottom", {"start": v(-203.2, -549.65) * mm, "end": v(0, -549.65) * mm});
            skLineSegment(sketch, "E88.top", {"start": v(-203.2, -653.1) * mm, "end": v(0, -653.1) * mm});
            skLineSegment(sketch, "E88.left", {"start": v(-203.2, -549.65) * mm, "end": v(-203.2, -653.1) * mm});
            skLineSegment(sketch, "E88.right", {"start": v(0, -584.2) * mm, "end": v(0, -653.1) * mm});
            skLineSegment(sketch, "E89.bottom", {"start": v(0, 0) * mm, "end": v(203.2, 0) * mm});
            skLineSegment(sketch, "E89.top", {"start": v(0, -105.15) * mm, "end": v(203.2, -105.15) * mm});
            skLineSegment(sketch, "E89.left", {"start": v(0, 0) * mm, "end": v(0, -105.15) * mm});
            skLineSegment(sketch, "E89.right", {"start": v(203.2, 0) * mm, "end": v(203.2, -105.15) * mm});
            skPoint(sketch, "E90", {"position": v(63.5, -526.85) * mm});
            skPoint(sketch, "E91", {"position": v(-63.5, -127.95) * mm});
            skSolve(sketch);
        }
        {
            var Q0;
            Q0 = qSketchRegion(id + "F12", true);
            var Q1;
            Q1=makeQuery(id+"F1.opExtrude","SWEPT_FACE",FACE,{"disambiguationData":[OSD([sQuery(id+"F0.wireOp",EDGE,"E5")])]});
            extrude(context, id + "F13", {"entities" : qUnion([Q0]), "operationType" : NewBodyOperationType.REMOVE, "oppositeDirection" : true, "depth" : 152.4 * mm});
        }
        {
            var Q0;
            Q0=makeQuery(id+"F9.opExtrude","SWEPT_FACE",FACE,{"disambiguationData":[OSD([sQuery(id+"F5.wireOp",EDGE,"E52")])]});
            var sketch = newSketch(context, id + "F14", { "sketchPlane" : qUnion([Q0])});
            skCircle(sketch, "E92", {"center": v(-76.2, -539.11) * mm, "radius": 4 * mm});
            skCircle(sketch, "E93.0.1.0", {"center": v(-76.2, -439.29) * mm, "radius": 4 * mm});
            skCircle(sketch, "E93.0.2.0", {"center": v(-76.2, -339.47) * mm, "radius": 4 * mm});
            skCircle(sketch, "E93.0.3.0", {"center": v(-76.2, -239.64) * mm, "radius": 4 * mm});
            skCircle(sketch, "E93.0.4.0", {"center": v(-76.2, -139.82) * mm, "radius": 4 * mm});
            skCircle(sketch, "E93.1.0.0", {"center": v(-136.53, -539.11) * mm, "radius": 4 * mm});
            skCircle(sketch, "E93.1.1.0", {"center": v(-136.53, -439.29) * mm, "radius": 4 * mm});
            skCircle(sketch, "E93.1.2.0", {"center": v(-136.53, -339.47) * mm, "radius": 4 * mm});
            skCircle(sketch, "E93.1.3.0", {"center": v(-136.53, -239.64) * mm, "radius": 4 * mm});
            skCircle(sketch, "E93.1.4.0", {"center": v(-136.53, -139.82) * mm, "radius": 4 * mm});
            skLineSegment(sketch, "E93.direction1", {"start": v(-76.2, -539.11) * mm, "end": v(-136.53, -539.11) * mm, "construction": true});
            skLineSegment(sketch, "E93.direction2", {"start": v(-76.2, -539.11) * mm, "end": v(-76.2, -439.29) * mm, "construction": true});
            skCircle(sketch, "E94", {"center": v(76.2, -115.7) * mm, "radius": 4 * mm});
            skCircle(sketch, "E95.0.1.0", {"center": v(76.2, -215.51) * mm, "radius": 4 * mm});
            skCircle(sketch, "E95.0.2.0", {"center": v(76.2, -315.34) * mm, "radius": 4 * mm});
            skCircle(sketch, "E95.0.3.0", {"center": v(76.2, -415.16) * mm, "radius": 4 * mm});
            skCircle(sketch, "E95.0.4.0", {"center": v(76.2, -514.98) * mm, "radius": 4 * mm});
            skCircle(sketch, "E95.1.0.0", {"center": v(136.52, -115.7) * mm, "radius": 4 * mm});
            skCircle(sketch, "E95.1.1.0", {"center": v(136.52, -215.51) * mm, "radius": 4 * mm});
            skCircle(sketch, "E95.1.2.0", {"center": v(136.52, -315.34) * mm, "radius": 4 * mm});
            skCircle(sketch, "E95.1.3.0", {"center": v(136.52, -415.16) * mm, "radius": 4 * mm});
            skCircle(sketch, "E95.1.4.0", {"center": v(136.52, -514.98) * mm, "radius": 4 * mm});
            skLineSegment(sketch, "E95.direction1", {"start": v(76.2, -115.7) * mm, "end": v(136.52, -115.7) * mm, "construction": true});
            skLineSegment(sketch, "E95.direction2", {"start": v(76.2, -115.7) * mm, "end": v(76.2, -215.51) * mm, "construction": true});
            skSolve(sketch);
        }
        {
            var Q0;
            Q0 = qSketchRegion(id + "F14", true);
            extrude(context, id + "F15", {"entities" : qUnion([Q0]), "operationType" : NewBodyOperationType.REMOVE, "oppositeDirection" : true, "depth" : 25.4 * mm});
        }
    });
